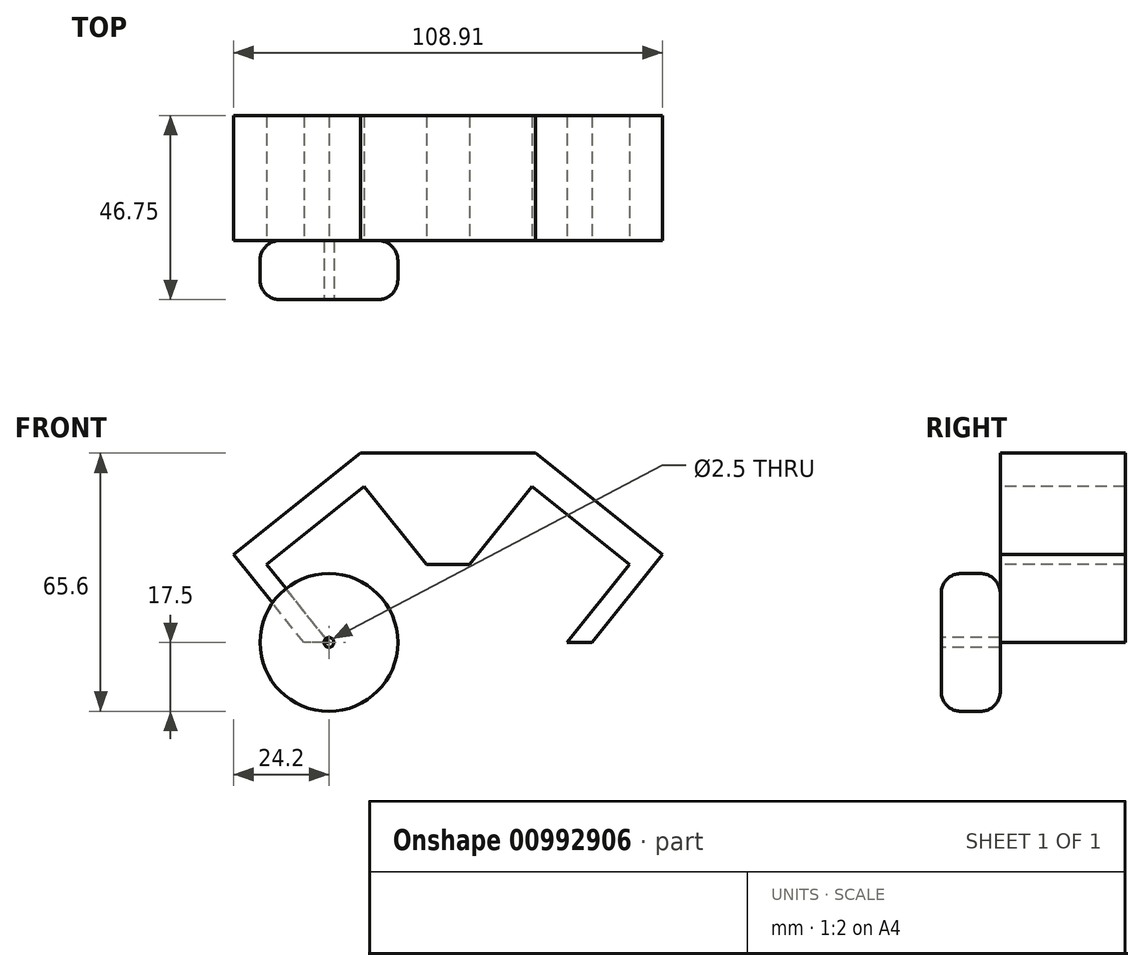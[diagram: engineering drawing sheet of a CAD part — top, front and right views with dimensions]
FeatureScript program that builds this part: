
annotation { "Feature Type Name" : "Feature", "Feature Type Description" : "" }
export const myFeature = defineFeature(function(context is Context, id is Id, definition is map)
    precondition{}
    {
        {
            var Q0;
            Q0=qCreatedBy(makeId("Front.planeOp"),FACE);
            var sketch = newSketch(context, id + "F0", { "sketchPlane" : qUnion([Q0])});
            skLineSegment(sketch, "E0", {"start": v(0, 0) * mm, "end": v(-15.87, 19.83) * mm});
            skLineSegment(sketch, "E1", {"start": v(-15.87, 19.83) * mm, "end": v(8.93, 39.67) * mm});
            skLineSegment(sketch, "E2", {"start": v(8.93, 39.67) * mm, "end": v(24.8, 19.83) * mm});
            skLineSegment(sketch, "E3", {"start": v(0, 0) * mm, "end": v(-6.35, 0) * mm});
            skLineSegment(sketch, "E4", {"start": v(-6.35, 0) * mm, "end": v(-24.2, 22.31) * mm});
            skLineSegment(sketch, "E5", {"start": v(-24.2, 22.31) * mm, "end": v(8.03, 48.1) * mm});
            skLineSegment(sketch, "E6", {"start": v(8.03, 48.1) * mm, "end": v(52.48, 48.1) * mm});
            skLineSegment(sketch, "E7", {"start": v(52.48, 48.1) * mm, "end": v(84.7, 22.31) * mm});
            skLineSegment(sketch, "E8", {"start": v(84.7, 22.31) * mm, "end": v(66.86, 0) * mm});
            skLineSegment(sketch, "E9", {"start": v(66.86, 0) * mm, "end": v(60.5, 0) * mm});
            skLineSegment(sketch, "E10", {"start": v(60.5, 0) * mm, "end": v(76.38, 19.83) * mm});
            skLineSegment(sketch, "E11", {"start": v(76.38, 19.83) * mm, "end": v(51.58, 39.67) * mm});
            skLineSegment(sketch, "E12", {"start": v(51.58, 39.67) * mm, "end": v(35.72, 19.83) * mm});
            skLineSegment(sketch, "E13", {"start": v(35.72, 19.83) * mm, "end": v(24.8, 19.83) * mm});
            skSolve(sketch);
        }
        {
            var Q0;
            Q0=makeQuery(id+"F0.imprint","IMPRINT",FACE,{"disambiguationData":[TD([[makeQuery(id+"F0.imprint","IMPRINT",EDGE,{"derivedFrom":sQuery(id+"F0.wireOp",EDGE,"E0")}),1.0]])]});
            extrude(context, id + "F1", {"entities" : qUnion([Q0]), "oppositeDirection" : true, "depth" : 31.75 * mm, "offsetDistance" : 25.4 * mm});
        }
        {
            var Q0;
            Q0=qCreatedBy(makeId("Front.planeOp"),FACE);
            var sketch = newSketch(context, id + "F2", { "sketchPlane" : qUnion([Q0])});
            skCircle(sketch, "E14", {"center": v(0, 0) * mm, "radius": 17.5 * mm});
            skSolve(sketch);
        }
        {
            var Q0;
            Q0=makeQuery(id+"F2.imprint","IMPRINT",FACE,{"disambiguationData":[TD([[makeQuery(id+"F2.imprint","IMPRINT",EDGE,{"derivedFrom":sQuery(id+"F2.wireOp",EDGE,"E14")}),1.0]])]});
            extrude(context, id + "F3", {"entities" : qUnion([Q0]), "depth" : 15 * mm, "offsetDistance" : 25 * mm});
        }
        {
            var Q0;
            Q0=makeQuery(id+"F3.opExtrude","CAP_EDGE",EDGE,{"disambiguationData":[OSD([sQuery(id+"F2.wireOp",EDGE,"E14")])],"isStart":false});
            var Q1;
            Q1=makeQuery(id+"F3.opExtrude","CAP_EDGE",EDGE,{"disambiguationData":[OSD([sQuery(id+"F2.wireOp",EDGE,"E14")])],"isStart":true});
            fillet(context, id + "F4", {"entities" : qUnion([Q0, Q1]), "radius" : 5 * mm, "tangentPropagation" : true, "allowEdgeOverflow" : false});
        }
        {
            var Q0;
            Q0=makeQuery(id+"F3.opExtrude","CAP_FACE",FACE,{"disambiguationData":[OSD([sQuery(id+"F2.wireOp",EDGE,"E14")])],"isStart":false});
            var sketch = newSketch(context, id + "F5", { "sketchPlane" : qUnion([Q0])});
            skCircle(sketch, "E15", {"center": v(0, 0) * mm, "radius": 1.25 * mm});
            skSolve(sketch);
        }
        {
            var Q0;
            Q0=makeQuery(id+"F5.imprint","IMPRINT",FACE,{"disambiguationData":[TD([[makeQuery(id+"F5.imprint","IMPRINT",EDGE,{"derivedFrom":sQuery(id+"F5.wireOp",EDGE,"E15")}),1.0]])]});
            extrude(context, id + "F6", {"entities" : qUnion([Q0]), "operationType" : NewBodyOperationType.REMOVE, "oppositeDirection" : true, "depth" : 15 * mm, "offsetDistance" : 25 * mm});
        }
    });
